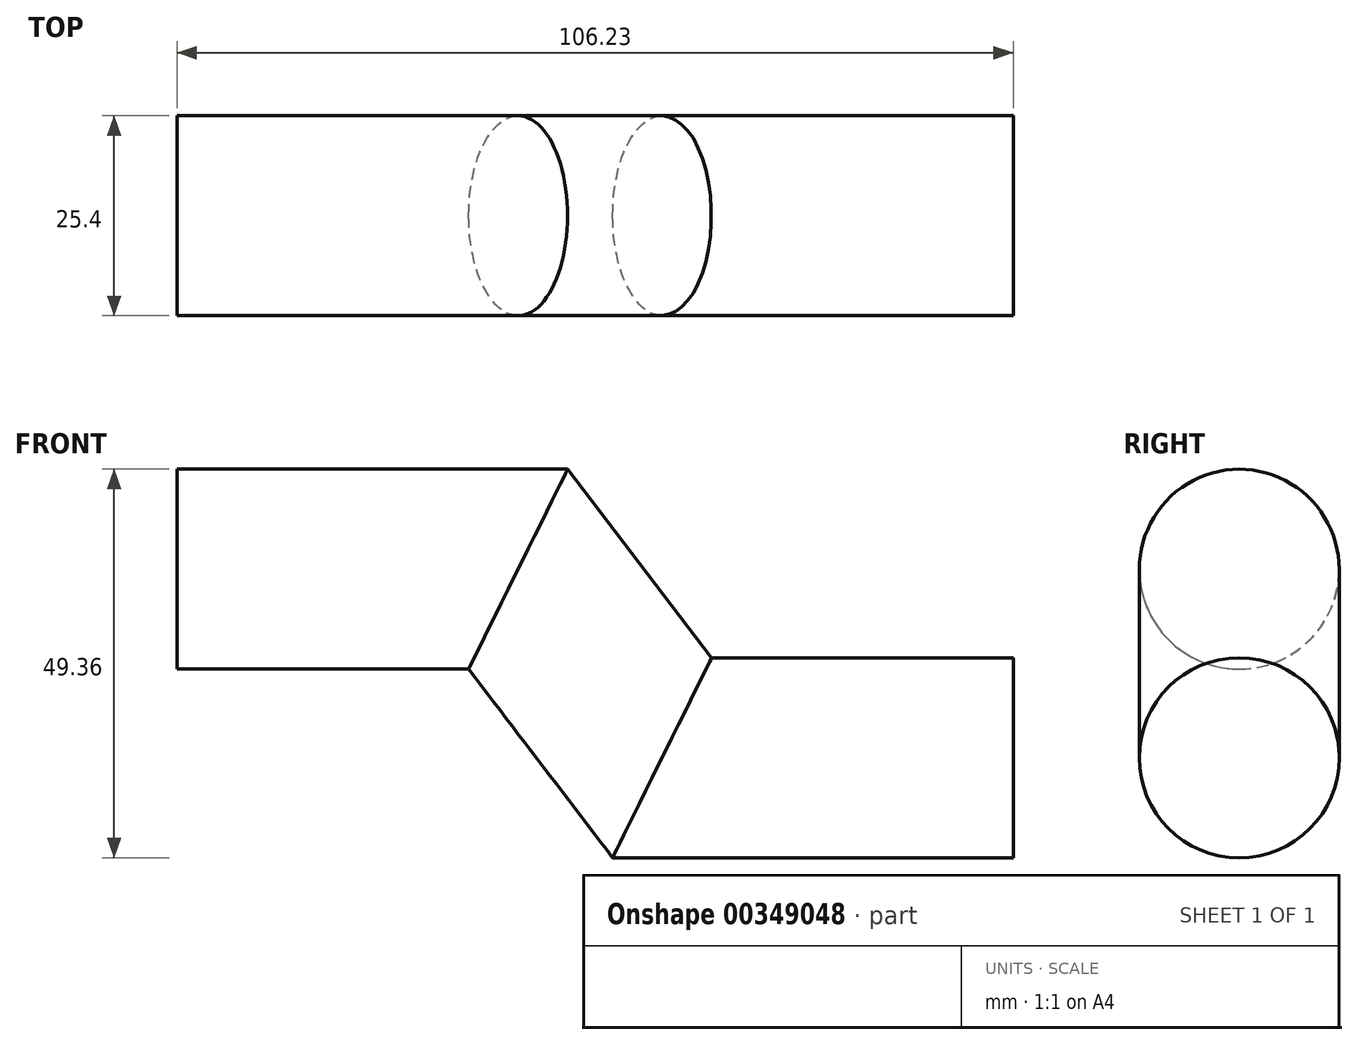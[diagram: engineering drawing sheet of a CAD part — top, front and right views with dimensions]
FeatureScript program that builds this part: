
annotation { "Feature Type Name" : "Feature", "Feature Type Description" : "" }
export const myFeature = defineFeature(function(context is Context, id is Id, definition is map)
    precondition{}
    {
        {
            var Q0;
            Q0=qCreatedBy(makeId("Right.planeOp"),FACE);
            var sketch = newSketch(context, id + "F0", { "sketchPlane" : qUnion([Q0])});
            skCircle(sketch, "E0", {"center": v(0, 0) * mm, "radius": 12.7 * mm});
            skSolve(sketch);
        }
        {
            var Q0;
            Q0=qCreatedBy(makeId("Front.planeOp"),FACE);
            var sketch = newSketch(context, id + "F1", { "sketchPlane" : qUnion([Q0])});
            skLineSegment(sketch, "E1", {"start": v(0.03, -0.24) * mm, "end": v(43.21, -0.24) * mm});
            skLineSegment(sketch, "E2", {"start": v(43.21, -0.24) * mm, "end": v(61.5, -24.2) * mm});
            skLineSegment(sketch, "E3", {"start": v(61.5, -24.2) * mm, "end": v(106.25, -24.2) * mm});
            skSolve(sketch);
        }
        {
            var Q0;
            Q0 = qSketchRegion(id + "F0", true);
            var Q1;
            Q1 = qConstructionFilter(qBodyType(qCreatedBy(id + "F1" ,EDGE), BodyType.WIRE), ConstructionObject.NO);
            sweep(context, id + "F2", {"profiles" : qUnion([Q0]), "path" : qUnion([Q1])});
        }
    });
